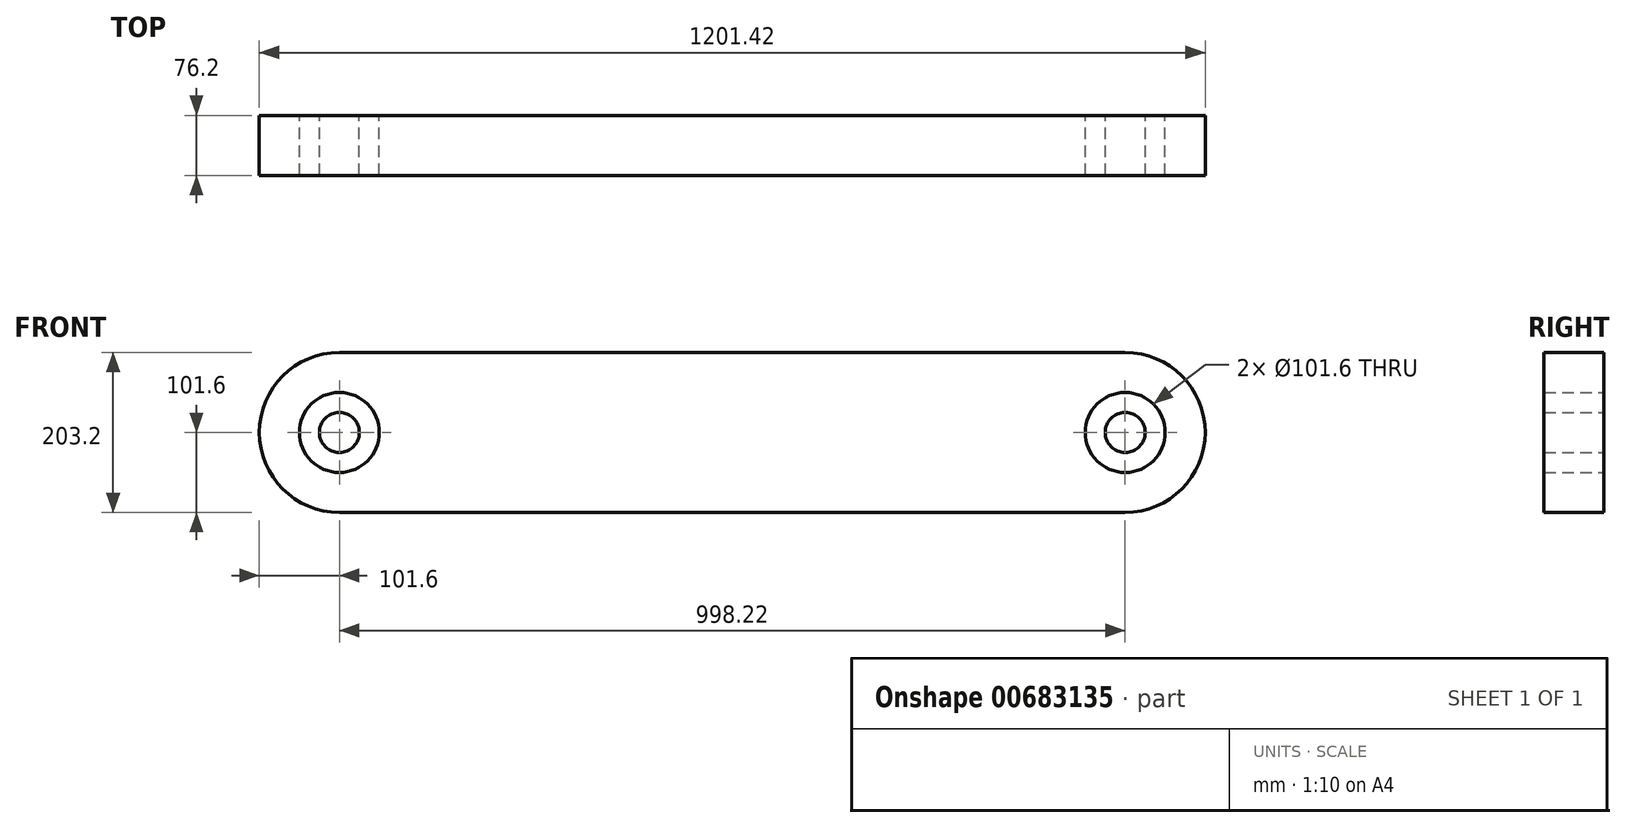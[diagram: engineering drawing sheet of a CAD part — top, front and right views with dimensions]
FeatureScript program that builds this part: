
annotation { "Feature Type Name" : "Feature", "Feature Type Description" : "" }
export const myFeature = defineFeature(function(context is Context, id is Id, definition is map)
    precondition{}
    {
        {
            var Q0;
            Q0=qCreatedBy(makeId("Front.planeOp"),FACE);
            var sketch = newSketch(context, id + "F0", { "sketchPlane" : qUnion([Q0])});
            skArc(sketch, "E0", {"start": v(0, 101.6) * mm, "mid": v(-101.6, 0) * mm, "end": v(0, -101.6) * mm});
            skArc(sketch, "E1", {"start": v(998.22, -101.6) * mm, "mid": v(1099.82, 0) * mm, "end": v(998.22, 101.6) * mm});
            skLineSegment(sketch, "E2", {"start": v(0, 101.6) * mm, "end": v(998.22, 101.6) * mm});
            skLineSegment(sketch, "E3", {"start": v(0, -101.6) * mm, "end": v(998.22, -101.6) * mm});
            skCircle(sketch, "E4", {"center": v(0, 0) * mm, "radius": 50.8 * mm});
            skCircle(sketch, "E5", {"center": v(998.22, 0) * mm, "radius": 50.8 * mm});
            skCircle(sketch, "E6", {"center": v(0, 0) * mm, "radius": 25.4 * mm});
            skCircle(sketch, "E7", {"center": v(998.22, 0) * mm, "radius": 25.4 * mm});
            skSolve(sketch);
        }
        {
            var Q0;
            Q0 = qSketchRegion(id + "F0", true);
            var Q1;
            Q1=makeQuery(id+"F0.imprint","IMPRINT",FACE,{"disambiguationData":[TD([[makeQuery(id+"F0.imprint","IMPRINT",EDGE,{"derivedFrom":sQuery(id+"F0.wireOp",EDGE,"E6")}),1.0]])]});
            var Q2;
            Q2=makeQuery(id+"F0.imprint","IMPRINT",FACE,{"disambiguationData":[TD([[makeQuery(id+"F0.imprint","IMPRINT",EDGE,{"derivedFrom":sQuery(id+"F0.wireOp",EDGE,"E7")}),1.0]])]});
            extrude(context, id + "F1", {"entities" : qUnion([Q0, Q1, Q2]), "depth" : 76.2 * mm, "offsetDistance" : 25.4 * mm});
        }
    });
